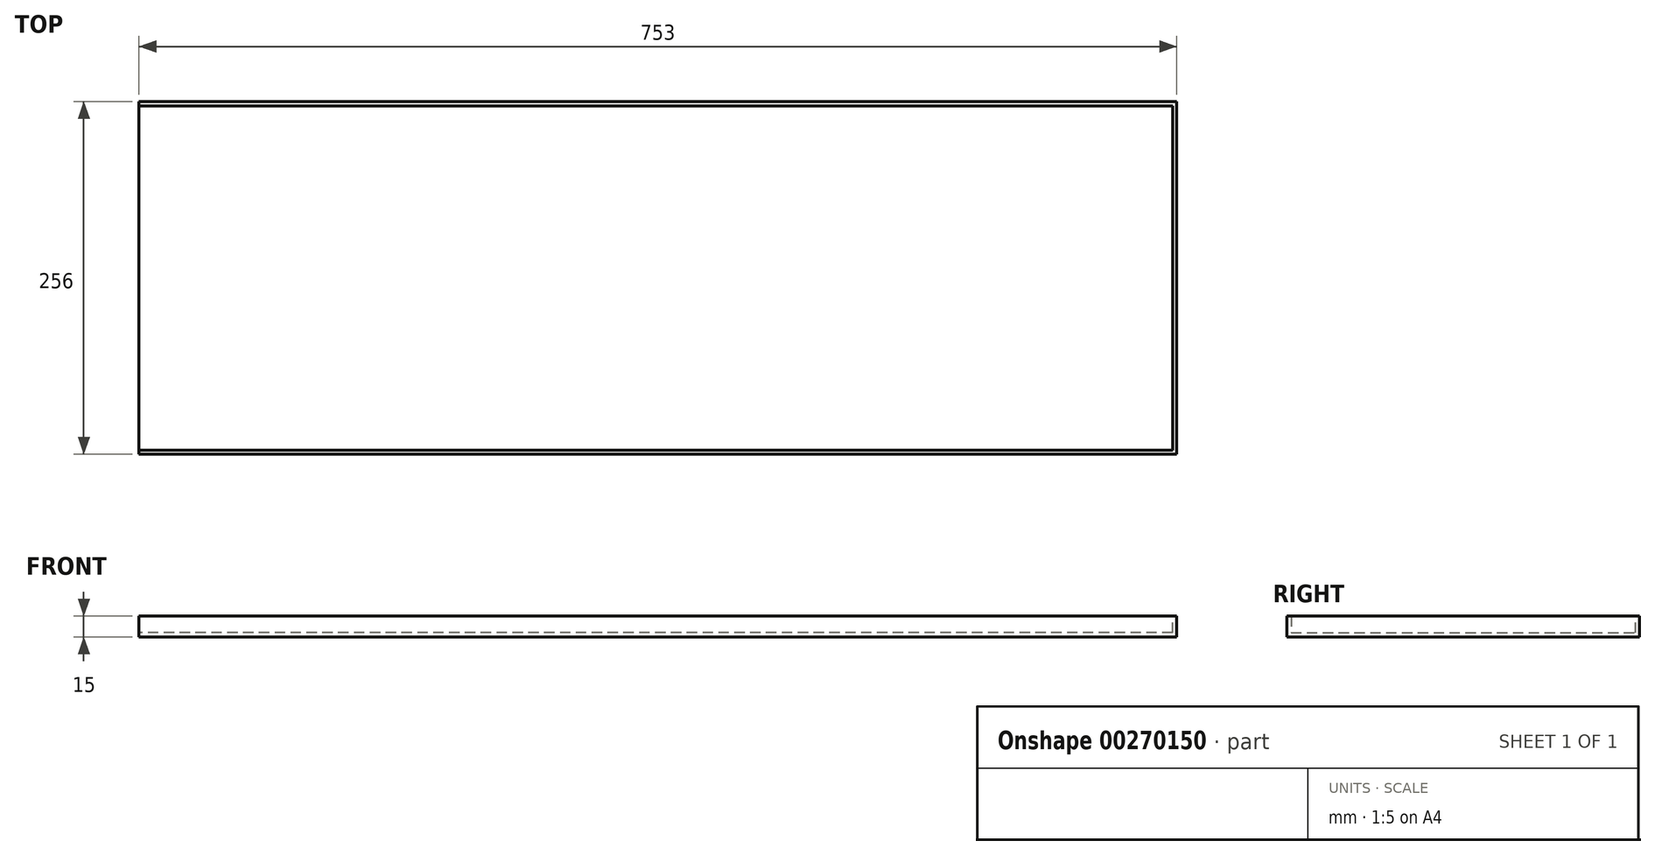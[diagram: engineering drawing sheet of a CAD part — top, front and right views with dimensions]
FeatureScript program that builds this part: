
annotation { "Feature Type Name" : "Feature", "Feature Type Description" : "" }
export const myFeature = defineFeature(function(context is Context, id is Id, definition is map)
    precondition{}
    {
        {
            var Q0;
            Q0=qCreatedBy(makeId("Right.planeOp"),FACE);
            var sketch = newSketch(context, id + "F0", { "sketchPlane" : qUnion([Q0])});
            skLineSegment(sketch, "E0", {"start": v(128, 0) * mm, "end": v(-128, 0) * mm});
            skLineSegment(sketch, "E1", {"start": v(-128, 0) * mm, "end": v(-128, 15) * mm});
            skLineSegment(sketch, "E2", {"start": v(-128, 15) * mm, "end": v(-125, 15) * mm});
            skLineSegment(sketch, "E3", {"start": v(-125, 15) * mm, "end": v(-125, 3) * mm});
            skLineSegment(sketch, "E4", {"start": v(-125, 3) * mm, "end": v(125, 3) * mm});
            skLineSegment(sketch, "E5", {"start": v(125, 3) * mm, "end": v(125, 15) * mm});
            skLineSegment(sketch, "E6", {"start": v(125, 15) * mm, "end": v(128, 15) * mm});
            skLineSegment(sketch, "E7", {"start": v(128, 15) * mm, "end": v(128, 0) * mm});
            skSolve(sketch);
        }
        {
            var Q0;
            Q0 = qSketchRegion(id + "F0", true);
            extrude(context, id + "F1", {"entities" : qUnion([Q0]), "depth" : 750 * mm});
        }
        {
            var Q0;
            Q0=makeQuery(id+"F1.opExtrude","CAP_FACE",FACE,{"disambiguationData":[OSD([sQuery(id+"F0.wireOp",EDGE,"E0"),sQuery(id+"F0.wireOp",EDGE,"E1"),sQuery(id+"F0.wireOp",EDGE,"E2"),sQuery(id+"F0.wireOp",EDGE,"E3"),sQuery(id+"F0.wireOp",EDGE,"E4"),sQuery(id+"F0.wireOp",EDGE,"E5"),sQuery(id+"F0.wireOp",EDGE,"E6"),sQuery(id+"F0.wireOp",EDGE,"E7")])],"isStart":false});
            var sketch = newSketch(context, id + "F2", { "sketchPlane" : qUnion([Q0])});
            skLineSegment(sketch, "E8.bottom", {"start": v(-128, 15) * mm, "end": v(128, 15) * mm});
            skLineSegment(sketch, "E8.top", {"start": v(-128, 0) * mm, "end": v(128, 0) * mm});
            skLineSegment(sketch, "E8.left", {"start": v(-128, 15) * mm, "end": v(-128, 0) * mm});
            skLineSegment(sketch, "E8.right", {"start": v(128, 15) * mm, "end": v(128, 0) * mm});
            skSolve(sketch);
        }
        {
            var Q0;
            Q0 = qSketchRegion(id + "F2", true);
            extrude(context, id + "F3", {"entities" : qUnion([Q0]), "operationType" : NewBodyOperationType.ADD, "depth" : 3 * mm});
        }
    });
